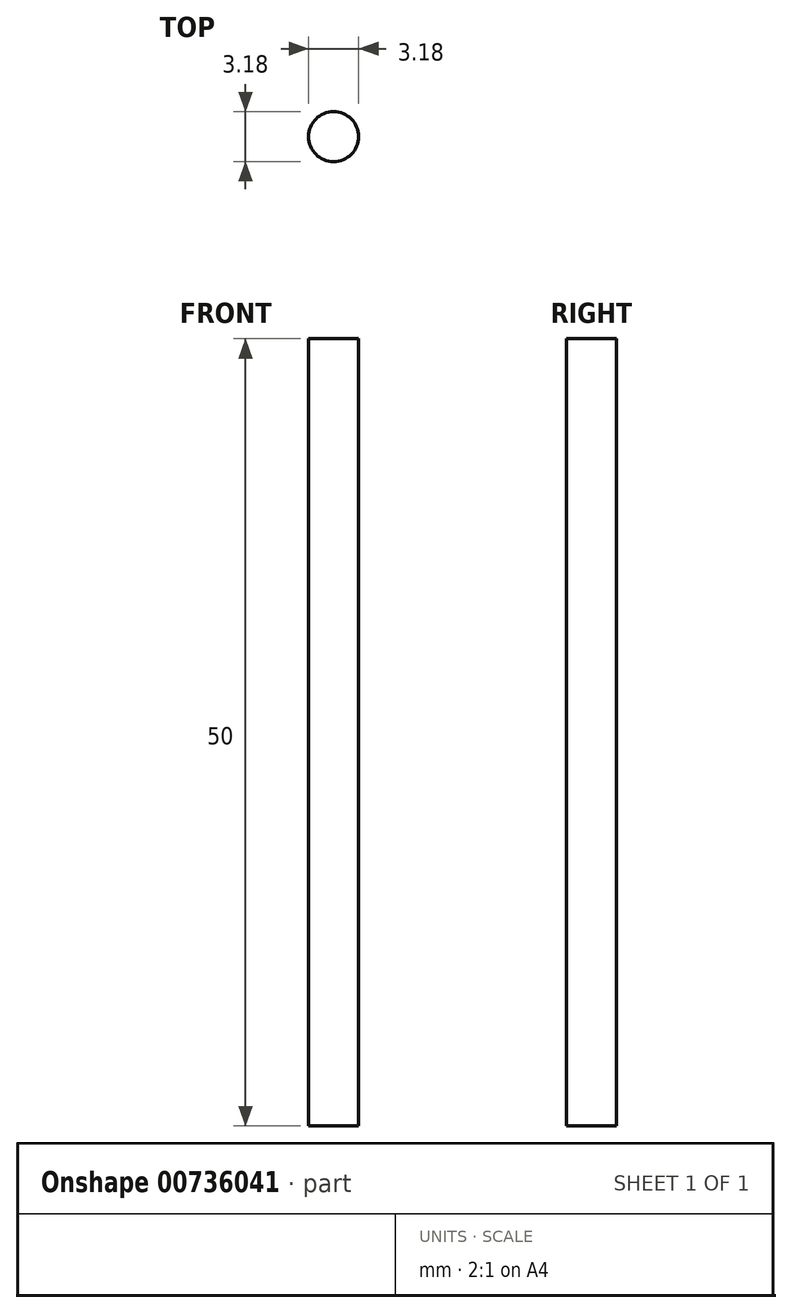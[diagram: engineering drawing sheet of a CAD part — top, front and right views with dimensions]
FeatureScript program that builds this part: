
annotation { "Feature Type Name" : "Feature", "Feature Type Description" : "" }
export const myFeature = defineFeature(function(context is Context, id is Id, definition is map)
    precondition{}
    {
        {
            var Q0;
            Q0=qCreatedBy(makeId("Top.planeOp"),FACE);
            var sketch = newSketch(context, id + "F0", { "sketchPlane" : qUnion([Q0])});
            skCircle(sketch, "E0", {"center": v(0, 0) * mm, "radius": 1.59 * mm});
            skSolve(sketch);
        }
        {
            var Q0;
            Q0 = qSketchRegion(id + "F0", true);
            extrude(context, id + "F1", {"entities" : qUnion([Q0]), "depth" : 50 * mm, "offsetDistance" : 25 * mm});
        }
    });
